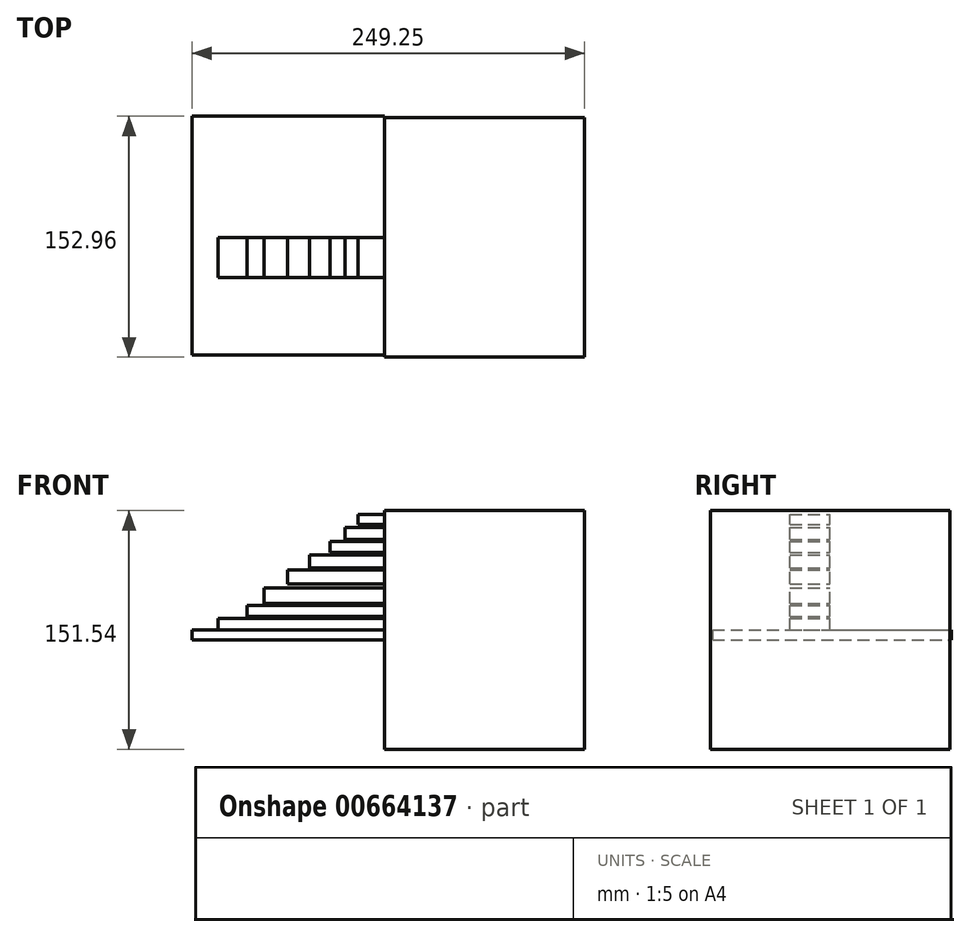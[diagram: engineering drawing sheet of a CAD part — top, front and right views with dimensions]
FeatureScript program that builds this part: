
annotation { "Feature Type Name" : "Feature", "Feature Type Description" : "" }
export const myFeature = defineFeature(function(context is Context, id is Id, definition is map)
    precondition{}
    {
        {
            var Q0;
            Q0=qCreatedBy(makeId("Right.planeOp"),FACE);
            var sketch = newSketch(context, id + "F0", { "sketchPlane" : qUnion([Q0])});
            skLineSegment(sketch, "E0.bottom", {"start": v(-75.92, -75.77) * mm, "end": v(76.24, -75.77) * mm});
            skLineSegment(sketch, "E0.top", {"start": v(-75.92, 75.77) * mm, "end": v(76.24, 75.77) * mm});
            skLineSegment(sketch, "E0.left", {"start": v(-75.92, -75.77) * mm, "end": v(-75.92, 75.77) * mm});
            skLineSegment(sketch, "E0.right", {"start": v(76.24, -75.77) * mm, "end": v(76.24, 75.77) * mm});
            skSolve(sketch);
        }
        {
            var Q0;
            Q0 = qSketchRegion(id + "F0", true);
            extrude(context, id + "F1", {"entities" : qUnion([Q0]), "depth" : 127 * mm, "offsetDistance" : 25.4 * mm});
        }
        {
            var Q0;
            Q0=makeQuery(id+"F1.opExtrude","SWEPT_FACE",FACE,{"disambiguationData":[OSD([sQuery(id+"F0.wireOp",EDGE,"E0.left")])]});
            extrude(context, id + "F2", {"entities" : qUnion([Q0]), "depth" : 101.6 * mm, "offsetDistance" : 25.4 * mm});
        }
        {
            var Q0;
            Q0=makeQuery(id+"F2.opExtrude","SWEPT_BODY",BODY,{"disambiguationData":[OSD([sQuery(id+"F0.wireOp",EDGE,"E0.left")])]});
            deleteBodies(context, id + "F3", {"entities" : qUnion([Q0])});
        }
        {
            var Q0;
            Q0=qCreatedBy(makeId("Top.planeOp"),FACE);
            var sketch = newSketch(context, id + "F4", { "sketchPlane" : qUnion([Q0])});
            skLineSegment(sketch, "E1.bottom", {"start": v(0, -74.49) * mm, "end": v(-122.25, -74.49) * mm});
            skLineSegment(sketch, "E1.top", {"start": v(0, 77.04) * mm, "end": v(-122.25, 77.04) * mm});
            skLineSegment(sketch, "E1.left", {"start": v(0, -74.49) * mm, "end": v(0, 77.04) * mm});
            skLineSegment(sketch, "E1.right", {"start": v(-122.25, -74.49) * mm, "end": v(-122.25, 77.04) * mm});
            skSolve(sketch);
        }
        {
            var Q0;
            Q0 = qSketchRegion(id + "F4", true);
            extrude(context, id + "F5", {"entities" : qUnion([Q0]), "operationType" : NewBodyOperationType.ADD, "oppositeDirection" : true, "depth" : 6.35 * mm, "offsetDistance" : 25.4 * mm});
        }
        {
            var Q0;
            Q0=qCreatedBy(makeId("Front.planeOp"),FACE);
            var sketch = newSketch(context, id + "F6", { "sketchPlane" : qUnion([Q0])});
            skLineSegment(sketch, "E2.bottom", {"start": v(-105.61, 0) * mm, "end": v(0, 0) * mm});
            skLineSegment(sketch, "E2.top", {"start": v(-105.61, 7.23) * mm, "end": v(0, 7.23) * mm});
            skLineSegment(sketch, "E2.left", {"start": v(-105.61, 0) * mm, "end": v(-105.61, 7.23) * mm});
            skLineSegment(sketch, "E2.right", {"start": v(0, 0) * mm, "end": v(0, 7.23) * mm});
            skSolve(sketch);
        }
        {
            var Q0;
            Q0 = qSketchRegion(id + "F6", true);
            extrude(context, id + "F7", {"entities" : qUnion([Q0]), "operationType" : NewBodyOperationType.ADD, "depth" : 25.4 * mm, "offsetDistance" : 25.4 * mm});
        }
        {
            var Q0;
            Q0=qCreatedBy(makeId("Front.planeOp"),FACE);
            var sketch = newSketch(context, id + "F8", { "sketchPlane" : qUnion([Q0])});
            skLineSegment(sketch, "E3.bottom", {"start": v(-87.38, 8.49) * mm, "end": v(0, 8.49) * mm});
            skLineSegment(sketch, "E3.top", {"start": v(-87.38, 15.4) * mm, "end": v(0, 15.4) * mm});
            skLineSegment(sketch, "E3.left", {"start": v(-87.38, 8.49) * mm, "end": v(-87.38, 15.4) * mm});
            skLineSegment(sketch, "E3.right", {"start": v(0, 8.49) * mm, "end": v(0, 15.4) * mm});
            skSolve(sketch);
        }
        {
            var Q0;
            Q0 = qSketchRegion(id + "F8", true);
            extrude(context, id + "F9", {"entities" : qUnion([Q0]), "operationType" : NewBodyOperationType.ADD, "depth" : 25.4 * mm, "offsetDistance" : 25.4 * mm});
        }
        {
            var Q0;
            Q0=qCreatedBy(makeId("Front.planeOp"),FACE);
            var sketch = newSketch(context, id + "F10", { "sketchPlane" : qUnion([Q0])});
            skLineSegment(sketch, "E4.bottom", {"start": v(0, 16.66) * mm, "end": v(-76.7, 16.66) * mm});
            skLineSegment(sketch, "E4.top", {"start": v(0, 26.72) * mm, "end": v(-76.7, 26.72) * mm});
            skLineSegment(sketch, "E4.left", {"start": v(0, 16.66) * mm, "end": v(0, 26.72) * mm});
            skLineSegment(sketch, "E4.right", {"start": v(-76.7, 16.66) * mm, "end": v(-76.7, 26.72) * mm});
            skLineSegment(sketch, "E5.bottom", {"start": v(-76.7, 16.66) * mm, "end": v(0, 16.66) * mm});
            skLineSegment(sketch, "E5.top", {"start": v(-76.7, 26.72) * mm, "end": v(0, 26.72) * mm});
            skSolve(sketch);
        }
        {
            var Q0;
            Q0=qCreatedBy(makeId("Front.planeOp"),FACE);
            var sketch = newSketch(context, id + "F11", { "sketchPlane" : qUnion([Q0])});
            skLineSegment(sketch, "E6.bottom", {"start": v(-61.6, 29.24) * mm, "end": v(0, 29.24) * mm});
            skLineSegment(sketch, "E6.top", {"start": v(-61.6, 38.04) * mm, "end": v(0, 38.04) * mm});
            skLineSegment(sketch, "E6.left", {"start": v(-61.6, 29.24) * mm, "end": v(-61.6, 38.04) * mm});
            skLineSegment(sketch, "E6.right", {"start": v(0, 29.24) * mm, "end": v(0, 38.04) * mm});
            skSolve(sketch);
        }
        {
            var Q0;
            Q0 = qSketchRegion(id + "F11", true);
            extrude(context, id + "F12", {"entities" : qUnion([Q0]), "operationType" : NewBodyOperationType.ADD, "depth" : 25.4 * mm, "offsetDistance" : 25.4 * mm});
        }
        {
            var Q0;
            Q0=qCreatedBy(makeId("Front.planeOp"),FACE);
            var sketch = newSketch(context, id + "F13", { "sketchPlane" : qUnion([Q0])});
            skLineSegment(sketch, "E7.bottom", {"start": v(-47.77, 39.3) * mm, "end": v(0, 39.3) * mm});
            skLineSegment(sketch, "E7.top", {"start": v(-47.77, 47.47) * mm, "end": v(0, 47.47) * mm});
            skLineSegment(sketch, "E7.left", {"start": v(-47.77, 39.3) * mm, "end": v(-47.77, 47.47) * mm});
            skLineSegment(sketch, "E7.right", {"start": v(0, 39.3) * mm, "end": v(0, 47.47) * mm});
            skSolve(sketch);
        }
        {
            var Q0;
            Q0 = qSketchRegion(id + "F13", true);
            extrude(context, id + "F14", {"entities" : qUnion([Q0]), "operationType" : NewBodyOperationType.ADD, "depth" : 25.4 * mm, "offsetDistance" : 25.4 * mm});
        }
        {
            var Q0;
            Q0=qCreatedBy(makeId("Front.planeOp"),FACE);
            var sketch = newSketch(context, id + "F15", { "sketchPlane" : qUnion([Q0])});
            skLineSegment(sketch, "E8.bottom", {"start": v(-34.56, 49.36) * mm, "end": v(0, 49.36) * mm});
            skLineSegment(sketch, "E8.top", {"start": v(-34.56, 56.27) * mm, "end": v(0, 56.27) * mm});
            skLineSegment(sketch, "E8.left", {"start": v(-34.56, 49.36) * mm, "end": v(-34.56, 56.27) * mm});
            skLineSegment(sketch, "E8.right", {"start": v(0, 49.36) * mm, "end": v(0, 56.27) * mm});
            skSolve(sketch);
        }
        {
            var Q0;
            Q0 = qSketchRegion(id + "F15", true);
            extrude(context, id + "F16", {"entities" : qUnion([Q0]), "operationType" : NewBodyOperationType.ADD, "depth" : 25.4 * mm, "offsetDistance" : 25.4 * mm});
        }
        {
            var Q0;
            Q0=qCreatedBy(makeId("Front.planeOp"),FACE);
            var sketch = newSketch(context, id + "F17", { "sketchPlane" : qUnion([Q0])});
            skLineSegment(sketch, "E9.bottom", {"start": v(-25.13, 57.53) * mm, "end": v(0, 57.53) * mm});
            skLineSegment(sketch, "E9.top", {"start": v(-25.13, 65.08) * mm, "end": v(0, 65.08) * mm});
            skLineSegment(sketch, "E9.left", {"start": v(-25.13, 57.53) * mm, "end": v(-25.13, 65.08) * mm});
            skLineSegment(sketch, "E9.right", {"start": v(0, 57.53) * mm, "end": v(0, 65.08) * mm});
            skSolve(sketch);
        }
        {
            var Q0;
            Q0 = qSketchRegion(id + "F17", true);
            extrude(context, id + "F18", {"entities" : qUnion([Q0]), "operationType" : NewBodyOperationType.ADD, "depth" : 25.4 * mm, "offsetDistance" : 25.4 * mm});
        }
        {
            var Q0;
            Q0=qCreatedBy(makeId("Front.planeOp"),FACE);
            var sketch = newSketch(context, id + "F19", { "sketchPlane" : qUnion([Q0])});
            skLineSegment(sketch, "E10.bottom", {"start": v(-16.96, 66.96) * mm, "end": v(0, 66.96) * mm});
            skLineSegment(sketch, "E10.top", {"start": v(-16.96, 73.25) * mm, "end": v(0, 73.25) * mm});
            skLineSegment(sketch, "E10.left", {"start": v(-16.96, 66.96) * mm, "end": v(-16.96, 73.25) * mm});
            skLineSegment(sketch, "E10.right", {"start": v(0, 66.96) * mm, "end": v(0, 73.25) * mm});
            skSolve(sketch);
        }
        {
            var Q0;
            Q0 = qSketchRegion(id + "F19", true);
            extrude(context, id + "F20", {"entities" : qUnion([Q0]), "operationType" : NewBodyOperationType.ADD, "depth" : 25.4 * mm, "offsetDistance" : 25.4 * mm});
        }
        {
            var Q0;
            Q0 = qSketchRegion(id + "F10", true);
            extrude(context, id + "F21", {"entities" : qUnion([Q0]), "operationType" : NewBodyOperationType.ADD, "depth" : 25.4 * mm, "offsetDistance" : 25.4 * mm});
        }
    });
